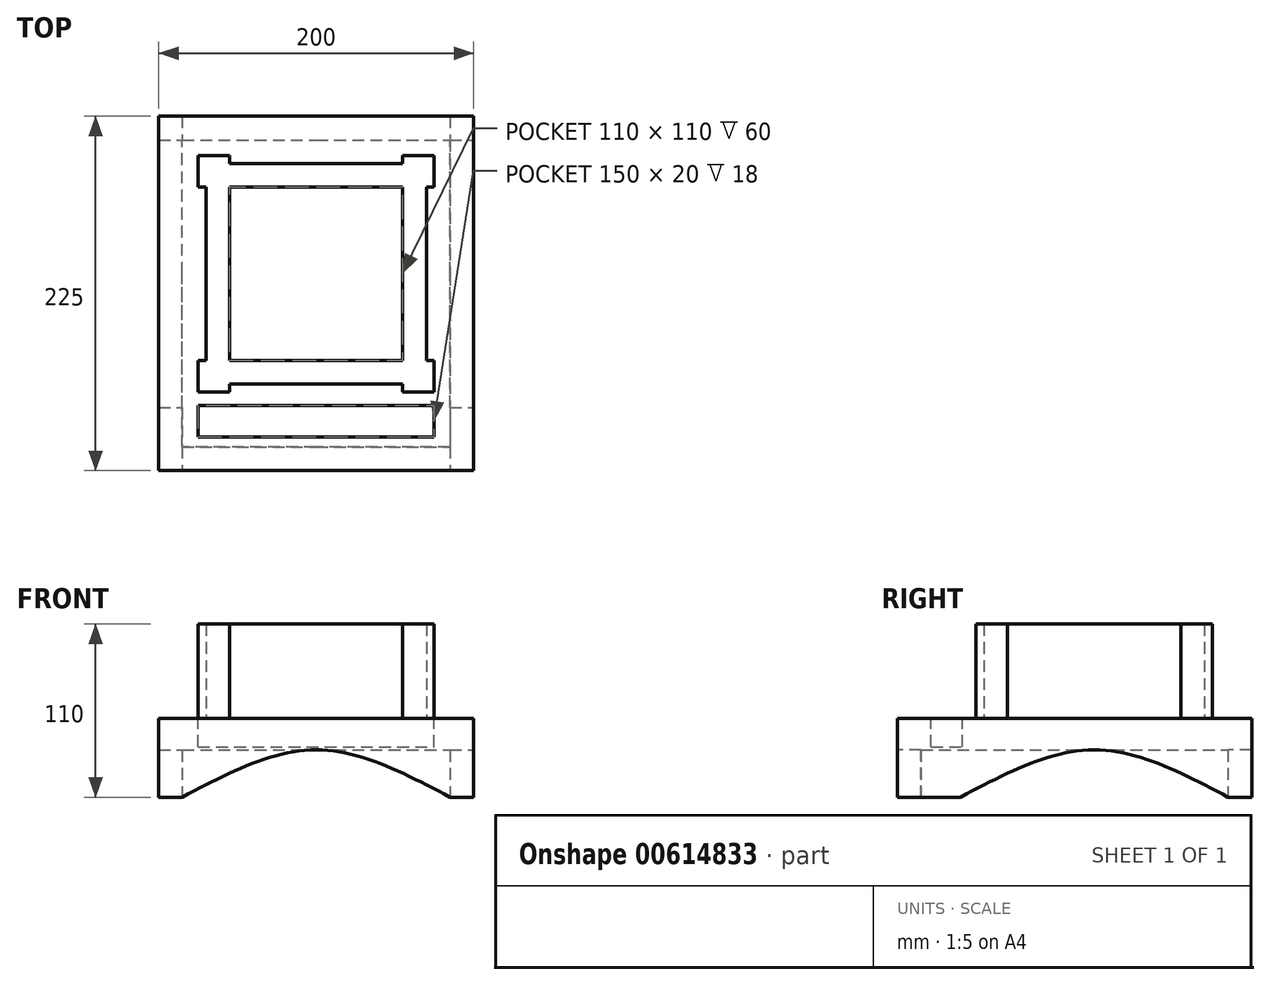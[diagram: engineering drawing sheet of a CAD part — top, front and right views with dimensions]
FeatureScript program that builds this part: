
annotation { "Feature Type Name" : "Feature", "Feature Type Description" : "" }
export const myFeature = defineFeature(function(context is Context, id is Id, definition is map)
    precondition{}
    {
        {
            var Q0;
            Q0=qCreatedBy(makeId("Top.planeOp"),FACE);
            var sketch = newSketch(context, id + "F0", { "sketchPlane" : qUnion([Q0])});
            skLineSegment(sketch, "E0.bottom", {"start": v(-151.08, 158.42) * mm, "end": v(48.92, 158.42) * mm});
            skLineSegment(sketch, "E0.top", {"start": v(-151.08, -41.58) * mm, "end": v(48.92, -41.58) * mm});
            skLineSegment(sketch, "E0.left", {"start": v(-151.08, 158.42) * mm, "end": v(-151.08, -41.58) * mm});
            skLineSegment(sketch, "E0.right", {"start": v(48.92, 158.42) * mm, "end": v(48.92, -41.58) * mm});
            skSolve(sketch);
        }
        {
            var Q0;
            Q0=makeQuery(id+"F0.imprint","IMPRINT",FACE,{"disambiguationData":[TD([[makeQuery(id+"F0.imprint","IMPRINT",EDGE,{"derivedFrom":sQuery(id+"F0.wireOp",EDGE,"E0.bottom")}),-1.0]])]});
            extrude(context, id + "F1", {"entities" : qUnion([Q0]), "depth" : 50 * mm, "offsetDistance" : 25 * mm});
        }
        {
            var Q0;
            Q0=makeQuery(id+"F1.opExtrude","SWEPT_FACE",FACE,{"disambiguationData":[OSD([sQuery(id+"F0.wireOp",EDGE,"E0.top")])]});
            var sketch = newSketch(context, id + "F2", { "sketchPlane" : qUnion([Q0])});
            skLineSegment(sketch, "E1", {"start": v(-151.08, 0) * mm, "end": v(-136.08, 0) * mm});
            skLineSegment(sketch, "E2", {"start": v(48.92, 0) * mm, "end": v(33.92, 0) * mm});
            skLineSegment(sketch, "E3", {"start": v(33.92, 0) * mm, "end": v(-51.08, 0) * mm});
            skLineSegment(sketch, "E4", {"start": v(-51.08, 0) * mm, "end": v(-51.08, 30) * mm});
            skPoint(sketch, "E4.endSnap0", {"position": v(-51.08, 50) * mm});
            skFitSpline(sketch, "E5", {"points": [v(-136.08, 0) * mm, v(-51.08, 30) * mm, v(33.92, 0) * mm], "startDerivative": vector(170, 90) * mm, "endDerivative": vector(170, -90) * mm});
            skSolve(sketch);
        }
        {
            var Q0;
            Q0=makeQuery(id+"F1.opExtrude","CAP_FACE",FACE,{"disambiguationData":[OSD([sQuery(id+"F0.wireOp",EDGE,"E0.bottom"),sQuery(id+"F0.wireOp",EDGE,"E0.top"),sQuery(id+"F0.wireOp",EDGE,"E0.left"),sQuery(id+"F0.wireOp",EDGE,"E0.right")])],"isStart":true});
            var sketch = newSketch(context, id + "F3", { "sketchPlane" : qUnion([Q0])});
            skLineSegment(sketch, "E6.0", {"start": v(-136.08, 26.58) * mm, "end": v(-136.08, -143.42) * mm});
            skLineSegment(sketch, "E6.1", {"start": v(33.92, 26.58) * mm, "end": v(-136.08, 26.58) * mm});
            skLineSegment(sketch, "E6.2", {"start": v(33.92, -143.42) * mm, "end": v(33.92, 26.58) * mm});
            skLineSegment(sketch, "E6.3", {"start": v(-136.08, -143.42) * mm, "end": v(33.92, -143.42) * mm});
            skSolve(sketch);
        }
        {
            var Q0;
            Q0=makeQuery(id+"F3.imprint","IMPRINT",FACE,{"disambiguationData":[TD([[makeQuery(id+"F3.imprint","IMPRINT",EDGE,{"derivedFrom":sQuery(id+"F3.wireOp",EDGE,"E6.0")}),1.0]])]});
            extrude(context, id + "F4", {"entities" : qUnion([Q0]), "operationType" : NewBodyOperationType.REMOVE, "oppositeDirection" : true, "depth" : 30 * mm, "offsetDistance" : 25 * mm});
        }
        {
            var Q0;
            {var subQ0=sQuery(id+"F2.wireOp",EDGE,"E4");Q0=makeQuery(id+"F2.imprint","IMPRINT",FACE,{"disambiguationData":[TD([[makeQuery(id+"F2.imprint","IMPRINT",EDGE,{"derivedFrom":subQ0}),1.0]])]});}
            var Q1;
            {var subQ0=sQuery(id+"F2.wireOp",EDGE,"E3");Q1=makeQuery(id+"F2.imprint","IMPRINT",FACE,{"disambiguationData":[TD([[makeQuery(id+"F2.imprint","IMPRINT",EDGE,{"derivedFrom":subQ0}),1.0]])]});}
            var Q2;
            Q2=makeQuery(id+"F1.opExtrude","SWEPT_FACE",FACE,{"disambiguationData":[OSD([sQuery(id+"F0.wireOp",EDGE,"E0.bottom")])]});
            extrude(context, id + "F5", {"entities" : qUnion([Q0, Q1]), "operationType" : NewBodyOperationType.REMOVE, "endBound" : BoundingType.UP_TO_SURFACE, "oppositeDirection" : true, "depth" : 25 * mm, "endBoundEntityFace" : qUnion([Q2]), "offsetDistance" : 25 * mm});
        }
        {
            var Q0;
            Q0=makeQuery(id+"F1.opExtrude","SWEPT_FACE",FACE,{"disambiguationData":[OSD([sQuery(id+"F0.wireOp",EDGE,"E0.right")])]});
            var sketch = newSketch(context, id + "F6", { "sketchPlane" : qUnion([Q0])});
            skLineSegment(sketch, "E7", {"start": v(-41.58, 0) * mm, "end": v(-26.58, 0) * mm});
            skLineSegment(sketch, "E8", {"start": v(-26.58, 0) * mm, "end": v(158.42, 0) * mm});
            skLineSegment(sketch, "E9", {"start": v(158.42, 0) * mm, "end": v(143.42, 0) * mm});
            skLineSegment(sketch, "E10", {"start": v(143.42, 0) * mm, "end": v(58.42, 0) * mm});
            skLineSegment(sketch, "E11", {"start": v(58.42, 0) * mm, "end": v(58.42, 30) * mm});
            skFitSpline(sketch, "E12", {"points": [v(-26.58, 0) * mm, v(58.42, 30) * mm, v(143.42, 0) * mm], "startDerivative": vector(170, 90) * mm, "endDerivative": vector(170, -90) * mm});
            skSolve(sketch);
        }
        {
            var Q0;
            {var subQ0=sQuery(id+"F6.wireOp",EDGE,"E8");Q0=makeQuery(id+"F6.imprint","IMPRINT",FACE,{"disambiguationData":[TD([[makeQuery(id+"F6.imprint","IMPRINT",EDGE,{"derivedFrom":subQ0}),-1.0]])]});}
            var Q1;
            {var subQ0=sQuery(id+"F6.wireOp",EDGE,"E10");Q1=makeQuery(id+"F6.imprint","IMPRINT",FACE,{"disambiguationData":[TD([[makeQuery(id+"F6.imprint","IMPRINT",EDGE,{"derivedFrom":subQ0}),-1.0]])]});}
            var Q2;
            Q2=makeQuery(id+"F1.opExtrude","SWEPT_FACE",FACE,{"disambiguationData":[OSD([sQuery(id+"F0.wireOp",EDGE,"E0.left")])]});
            extrude(context, id + "F7", {"entities" : qUnion([Q0, Q1]), "operationType" : NewBodyOperationType.REMOVE, "endBound" : BoundingType.UP_TO_SURFACE, "oppositeDirection" : true, "depth" : 25 * mm, "endBoundEntityFace" : qUnion([Q2]), "offsetDistance" : 25 * mm});
        }
        {
            var Q0;
            Q0=makeQuery(id+"F1.opExtrude","CAP_FACE",FACE,{"disambiguationData":[OSD([sQuery(id+"F0.wireOp",EDGE,"E0.bottom"),sQuery(id+"F0.wireOp",EDGE,"E0.top"),sQuery(id+"F0.wireOp",EDGE,"E0.left"),sQuery(id+"F0.wireOp",EDGE,"E0.right")])],"isStart":false});
            var sketch = newSketch(context, id + "F8", { "sketchPlane" : qUnion([Q0])});
            skLineSegment(sketch, "E13.0", {"start": v(-121.08, 113.42) * mm, "end": v(-121.08, 3.42) * mm});
            skLineSegment(sketch, "E13.1", {"start": v(3.92, 128.42) * mm, "end": v(-106.08, 128.42) * mm});
            skLineSegment(sketch, "E13.2", {"start": v(18.92, 3.42) * mm, "end": v(18.92, 113.42) * mm});
            skLineSegment(sketch, "E13.3", {"start": v(-106.08, -11.58) * mm, "end": v(3.92, -11.58) * mm});
            skLineSegment(sketch, "E14.0", {"start": v(3.92, 113.42) * mm, "end": v(-106.08, 113.42) * mm});
            skLineSegment(sketch, "E14.1", {"start": v(3.92, 3.42) * mm, "end": v(3.92, 113.42) * mm});
            skLineSegment(sketch, "E14.2", {"start": v(-106.08, 3.42) * mm, "end": v(3.92, 3.42) * mm});
            skLineSegment(sketch, "E14.3", {"start": v(-106.08, 113.42) * mm, "end": v(-106.08, 3.42) * mm});
            skLineSegment(sketch, "E15", {"start": v(-106.08, -11.58) * mm, "end": v(-106.08, -16.58) * mm});
            skLineSegment(sketch, "E16", {"start": v(-106.08, -16.58) * mm, "end": v(-126.08, -16.58) * mm});
            skLineSegment(sketch, "E17", {"start": v(-126.08, -16.58) * mm, "end": v(-126.08, 3.42) * mm});
            skLineSegment(sketch, "E18", {"start": v(-126.08, 3.42) * mm, "end": v(-121.08, 3.42) * mm});
            skLineSegment(sketch, "E19", {"start": v(-106.08, 128.42) * mm, "end": v(-106.08, 133.42) * mm});
            skLineSegment(sketch, "E20", {"start": v(-106.08, 133.42) * mm, "end": v(-126.08, 133.42) * mm});
            skLineSegment(sketch, "E21", {"start": v(-126.08, 133.42) * mm, "end": v(-126.08, 113.42) * mm});
            skLineSegment(sketch, "E22", {"start": v(-126.08, 113.42) * mm, "end": v(-121.08, 113.42) * mm});
            skLineSegment(sketch, "E23", {"start": v(18.92, 113.42) * mm, "end": v(23.92, 113.42) * mm});
            skLineSegment(sketch, "E24", {"start": v(23.92, 113.42) * mm, "end": v(23.92, 133.42) * mm});
            skLineSegment(sketch, "E25", {"start": v(23.92, 133.42) * mm, "end": v(3.92, 133.42) * mm});
            skLineSegment(sketch, "E26", {"start": v(3.92, 133.42) * mm, "end": v(3.92, 128.42) * mm});
            skLineSegment(sketch, "E27", {"start": v(3.92, -11.58) * mm, "end": v(3.92, -16.58) * mm});
            skLineSegment(sketch, "E28", {"start": v(3.92, -16.58) * mm, "end": v(23.92, -16.58) * mm});
            skLineSegment(sketch, "E29", {"start": v(23.92, -16.58) * mm, "end": v(23.92, 3.42) * mm});
            skLineSegment(sketch, "E30", {"start": v(23.92, 3.42) * mm, "end": v(18.92, 3.42) * mm});
            skSolve(sketch);
        }
        {
            var Q0;
            Q0=makeQuery(id+"F8.imprint","IMPRINT",FACE,{"disambiguationData":[TD([[makeQuery(id+"F8.imprint","IMPRINT",EDGE,{"derivedFrom":sQuery(id+"F8.wireOp",EDGE,"E13.0")}),1.0]])]});
            extrude(context, id + "F9", {"entities" : qUnion([Q0]), "operationType" : NewBodyOperationType.ADD, "depth" : 60 * mm, "offsetDistance" : 25 * mm});
        }
        {
            var Q0;
            Q0=makeQuery(id+"F1.opExtrude","SWEPT_FACE",FACE,{"disambiguationData":[OSD([sQuery(id+"F0.wireOp",EDGE,"E0.top")])]});
            extrude(context, id + "F10", {"entities" : qUnion([Q0]), "operationType" : NewBodyOperationType.ADD, "depth" : 25 * mm, "offsetDistance" : 25 * mm});
        }
        {
            var Q0;
            {var subQ0=sQuery(id+"F3.wireOp",EDGE,"E6.1");var subQ1=makeQuery(id+"F4.boolean.opBoolean","COPY",FACE,{"derivedFrom":makeQuery(id+"F4.opExtrude","SWEPT_FACE",FACE,{"disambiguationData":[OSD([subQ0])]})});var subQ2=sQuery(id+"F3.wireOp",EDGE,"E6.0");Q0=makeQuery(id+"F5.boolean.opBoolean","SPLIT",FACE,{"disambiguationData":[TD([makeQuery(id+"F4.boolean.opBoolean","COPY",FACE,{"derivedFrom":makeQuery(id+"F4.opExtrude","SWEPT_FACE",FACE,{"disambiguationData":[OSD([subQ2])]})})])],"derivedFrom":subQ1});}
            var Q1;
            {var subQ0=sQuery(id+"F3.wireOp",EDGE,"E6.2");var subQ1=sQuery(id+"F3.wireOp",EDGE,"E6.1");var subQ2=makeQuery(id+"F4.boolean.opBoolean","COPY",FACE,{"derivedFrom":makeQuery(id+"F4.opExtrude","SWEPT_FACE",FACE,{"disambiguationData":[OSD([subQ1])]})});Q1=makeQuery(id+"F5.boolean.opBoolean","SPLIT",FACE,{"disambiguationData":[TD([makeQuery(id+"F4.boolean.opBoolean","COPY",FACE,{"derivedFrom":makeQuery(id+"F4.opExtrude","SWEPT_FACE",FACE,{"disambiguationData":[OSD([subQ0])]})})])],"derivedFrom":subQ2});}
            extrude(context, id + "F11", {"entities" : qUnion([Q0, Q1]), "operationType" : NewBodyOperationType.REMOVE, "oppositeDirection" : true, "depth" : 25 * mm, "offsetDistance" : 25 * mm});
        }
        {
            var Q0;
            {var subQ0=sQuery(id+"F0.wireOp",EDGE,"E0.top");var subQ1=sQuery(id+"F0.wireOp",EDGE,"E0.left");var subQ2=sQuery(id+"F0.wireOp",EDGE,"E0.right");var subQ3=sQuery(id+"F0.wireOp",EDGE,"E0.bottom");Q0=makeQuery(id+"F10.boolean.opBoolean","MERGE",FACE,{"derivedFrom":[makeQuery(id+"F9.boolean.opBoolean","SPLIT",FACE,{"disambiguationData":[TD([makeQuery(id+"F1.opExtrude","SWEPT_FACE",FACE,{"disambiguationData":[OSD([subQ3])]})])],"derivedFrom":makeQuery(id+"F1.opExtrude","CAP_FACE",FACE,{"disambiguationData":[OSD([subQ3,subQ0,subQ1,subQ2])],"isStart":false})}),makeQuery(id+"F10.opExtrude","SWEPT_FACE",FACE,{"disambiguationData":[OSD([subQ0]),TDD([makeQuery(id+"F1.opExtrude","CAP_EDGE",EDGE,{"disambiguationData":[OSD([subQ0])],"isStart":false})])]})]});}
            var sketch = newSketch(context, id + "F12", { "sketchPlane" : qUnion([Q0])});
            skLineSegment(sketch, "E31", {"start": v(-126.08, -25.19) * mm, "end": v(23.92, -25.19) * mm});
            skLineSegment(sketch, "E32", {"start": v(23.92, -25.19) * mm, "end": v(23.92, -45.19) * mm});
            skLineSegment(sketch, "E33", {"start": v(23.92, -45.19) * mm, "end": v(-126.08, -45.19) * mm});
            skLineSegment(sketch, "E34", {"start": v(-126.08, -45.19) * mm, "end": v(-126.08, -25.19) * mm});
            skSolve(sketch);
        }
        {
            var Q0;
            Q0=makeQuery(id+"F12.imprint","IMPRINT",FACE,{"disambiguationData":[TD([[makeQuery(id+"F12.imprint","IMPRINT",EDGE,{"derivedFrom":sQuery(id+"F12.wireOp",EDGE,"E31")}),-1.0]])]});
            extrude(context, id + "F13", {"entities" : qUnion([Q0]), "operationType" : NewBodyOperationType.REMOVE, "oppositeDirection" : true, "depth" : 18 * mm, "offsetDistance" : 25 * mm});
        }
    });
